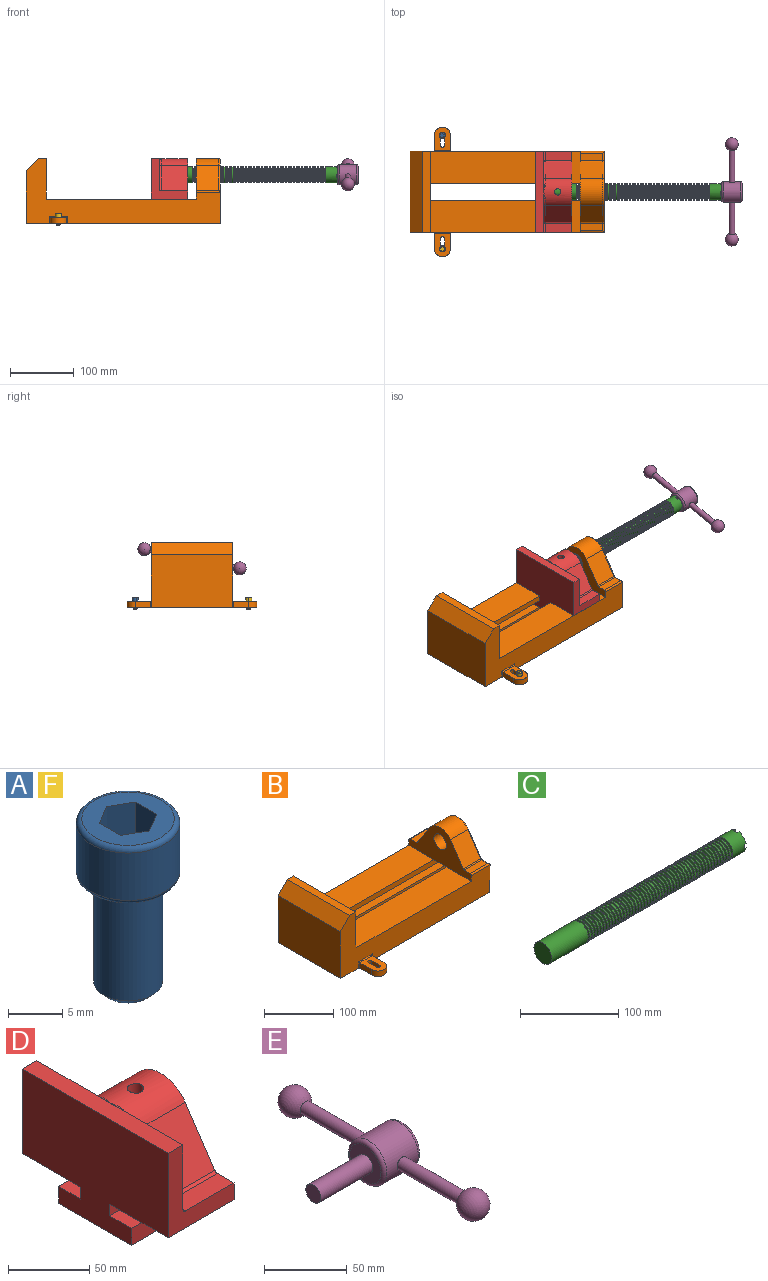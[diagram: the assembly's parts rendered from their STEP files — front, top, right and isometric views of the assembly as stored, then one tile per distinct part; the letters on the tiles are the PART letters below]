
ASSEMBLY  parts=6 mates=6
PART A: 15 faces, bbox 10.3x10.3x19.1 mm
  f0: plane 8.51x8.51mm, normal (0,0,1), area 37.2mm2, adj f5,f6,f7,f8,f9,f10,f14
  f1: cylinder r=3.17mm len=11.94mm, axis (0,0,1), area 238.2mm2, adj f4,f12
  f2: plane 4.83x4.83mm, normal (0,0,-1), area 18.3mm2, adj f12
  f3: cylinder r=4.76mm len=9.53mm, axis (0,0,-1), area 159.6mm2, adj f13,f14
  f4: plane 8.51x8.51mm, normal (0,0,-1), area 25.2mm2, adj f1,f13
  f5: plane 4.83x2.38mm, normal (-0.5,-0.87,0), area 13.3mm2, adj f0,f6,f10,f11
  f6: plane 4.83x2.38mm, normal (0.5,-0.87,0), area 13.3mm2, adj f0,f5,f7,f11
  f7: plane 4.83x2.75mm, normal (1,0,0), area 13.3mm2, adj f0,f6,f8,f11
  f8: plane 4.83x2.38mm, normal (0.5,0.87,0), area 13.3mm2, adj f0,f7,f9,f11
  f9: plane 4.83x2.38mm, normal (-0.5,0.87,0), area 13.3mm2, adj f0,f8,f10,f11
  f10: plane 4.83x2.75mm, normal (-1,0,0), area 13.3mm2, adj f0,f5,f9,f11
  f11: plane 5.5x4.76mm, normal (0,0,1), area 19.6mm2, adj f5,f6,f7,f8,f9,f10
  f12: cone r=3.17mm half-angle=45deg, axis (0,0,1), area 18.9mm2, adj f1,f2
  f13: torus R=4.25mm, axis (0,0,1), area 23mm2, adj f3,f4
  f14: torus R=4.25mm, axis (0,0,1), area 23mm2, adj f0,f3
PART B: 61 faces, bbox 304.8x203.2x103.7 mm
  f0: plane 304.8x101.6mm, normal (0,1,0), area 13520.3mm2, adj f3,f4,f5,f6,f7,f8,f9,f16
  f1: plane 304.8x101.6mm, normal (0,-1,0), area 13520.3mm2, adj f2,f3,f5,f6,f7,f8,f9,f16
  f2: plane 234.95x50.8mm, normal (0,0,1), area 11935.5mm2, adj f1,f5,f16,f26
  f3: plane 127x99.06mm, normal (1,0,0), area 7097.5mm2, adj f0,f1,f9,f14,f17,f18,f19,f20
  f4: plane 234.95x50.8mm, normal (0,0,1), area 11935.5mm2, adj f0,f5,f16,f27
  f5: plane 127x101.6mm, normal (1,0,0), area 9516.1mm2, adj f0,f1,f2,f4,f6,f9,f18,f19
  f6: plane 127x12.7mm, normal (0,0,1), area 1612.9mm2, adj f0,f1,f5,f7
  f7: plane 127x19.05mm, normal (-0.71,0,0.71), area 3421.5mm2, adj f0,f1,f6,f8
  f8: plane 127x82.55mm, normal (-1,0,0), area 10483.8mm2, adj f0,f1,f7,f9
  f9: plane 304.8x203.2mm, normal (0,0,-1), area 33298.3mm2, adj f0,f1,f3,f5,f8,f21,f22,f39
  f10: plane 35.56x11.98mm, normal (0,0,1), area 426mm2, adj f16,f28,f29,f30
  f11: plane 38.43x35.56mm, normal (0,0.83,0.56), area 1645.4mm2, adj f12,f16,f29,f32
  f12: cylinder r=25.4mm len=42.19mm, axis (1,0,0), area 1770.2mm2, adj f11,f13,f16,f33
  f13: plane 38.43x35.56mm, normal (0,-0.83,0.56), area 1645.4mm2, adj f12,f16,f34,f35
  f14: cylinder r=12.7mm len=38.1mm, axis (1,0,0), area 3040.2mm2, adj f3,f16
  f15: plane 35.56x11.98mm, normal (0,0,1), area 426mm2, adj f16,f34,f36,f38
  f16: plane 127x63.5mm, normal (-1,0,0), area 4155.5mm2, adj f0,f1,f2,f4,f10,f11,f12,f13
  f17: plane 38.1x25.4mm, normal (0,0,-1), area 967.7mm2, adj f3,f16,f26,f27
  f18: plane 273.05x19.05mm, normal (0,0,-1), area 5201.6mm2, adj f3,f5,f19,f26
  f19: plane 273.05x12.7mm, normal (0,1,0), area 3467.7mm2, adj f3,f5,f18,f20
  f20: plane 273.05x19.05mm, normal (0,0,1), area 5201.6mm2, adj f3,f5,f19,f21
  f21: plane 273.05x16.51mm, normal (0,1,0), area 4508.1mm2, adj f3,f5,f9,f20
  f22: plane 273.05x16.51mm, normal (0,-1,0), area 4508.1mm2, adj f3,f5,f9,f23
  f23: plane 273.05x19.05mm, normal (0,0,1), area 5201.6mm2, adj f3,f5,f22,f24
  f24: plane 273.05x12.7mm, normal (0,-1,0), area 3467.7mm2, adj f3,f5,f23,f25
  f25: plane 273.05x19.05mm, normal (0,0,-1), area 5201.6mm2, adj f3,f5,f24,f27
  f26: plane 273.05x8.89mm, normal (0,1,0), area 2427.4mm2, adj f2,f3,f5,f17,f18
  f27: plane 273.05x8.89mm, normal (0,-1,0), area 2427.4mm2, adj f3,f4,f5,f17,f25
  f28: cylinder r=2.54mm len=38.1mm, axis (1,0,0), area 148.3mm2, adj f0,f10,f16,f30
  f29: cylinder r=2.54mm len=35.56mm, axis (-1,0,0), area 88.5mm2, adj f10,f11,f16,f31
  f30: cylinder r=2.54mm len=14.52mm, axis (0,1,0), area 54.3mm2, adj f3,f10,f28,f31
  f31: torus R=5.08mm, axis (-1,0,0), area 13.5mm2, adj f3,f29,f30,f32
  f32: cylinder r=2.54mm len=39.84mm, axis (0,0.56,-0.83), area 184.6mm2, adj f3,f11,f31,f33
  f33: torus R=22.86mm, axis (-1,0,0), area 191.4mm2, adj f3,f12,f32,f35
  f34: cylinder r=2.54mm len=35.56mm, axis (-1,0,0), area 88.5mm2, adj f13,f15,f16,f37
  f35: cylinder r=2.54mm len=39.84mm, axis (0,0.56,0.83), area 184.6mm2, adj f3,f13,f33,f37
  f36: cylinder r=2.54mm len=38.1mm, axis (-1,0,0), area 148.3mm2, adj f1,f15,f16,f38
  f37: torus R=5.08mm, axis (-1,0,0), area 13.5mm2, adj f3,f34,f35,f38
  f38: cylinder r=2.54mm len=14.52mm, axis (0,1,0), area 54.3mm2, adj f3,f15,f36,f37
  f39: plane 23.88x9.53mm, normal (-1,0,0), area 227.4mm2, adj f9,f45,f46,f60
  f40: plane 23.88x9.53mm, normal (1,0,0), area 227.4mm2, adj f9,f45,f46,f58
  f41: cylinder r=3.3mm len=9.53mm, axis (0,0,-1), area 98.8mm2, adj f9,f42,f44,f46
  f42: plane 15.62x9.53mm, normal (-1,0,0), area 148.8mm2, adj f9,f41,f43,f46
  f43: cylinder r=3.3mm len=9.53mm, axis (0,0,-1), area 98.8mm2, adj f9,f42,f44,f46
  f44: plane 15.62x9.53mm, normal (1,0,0), area 148.8mm2, adj f9,f41,f43,f46
  f45: cylinder r=12.7mm len=25.4mm, axis (0,0,-1), area 380mm2, adj f9,f39,f40,f46
  f46: plane 36.58x25.4mm, normal (0,0,1), area 722.4mm2, adj f39,f40,f41,f42,f43,f44,f45,f59
  f47: plane 23.88x9.53mm, normal (-1,0,0), area 227.4mm2, adj f9,f53,f54,f56
  f48: plane 23.88x9.53mm, normal (1,0,0), area 227.4mm2, adj f9,f53,f54,f55
  f49: cylinder r=3.3mm len=9.53mm, axis (0,0,-1), area 98.8mm2, adj f9,f50,f52,f54
  f50: plane 15.62x9.53mm, normal (-1,0,0), area 148.8mm2, adj f9,f49,f51,f54
  f51: cylinder r=3.3mm len=9.53mm, axis (0,0,-1), area 98.8mm2, adj f9,f50,f52,f54
  f52: plane 15.62x9.53mm, normal (1,0,0), area 148.8mm2, adj f9,f49,f51,f54
  f53: cylinder r=12.7mm len=25.4mm, axis (0,0,-1), area 380mm2, adj f9,f47,f48,f54
  f54: plane 36.58x25.4mm, normal (0,0,1), area 722.4mm2, adj f47,f48,f49,f50,f51,f52,f53,f57
  f55: cylinder r=1.52mm len=11.05mm, axis (0,0,-1), area 24.1mm2, adj f0,f9,f48,f57
  f56: cylinder r=1.52mm len=11.05mm, axis (0,0,1), area 24.1mm2, adj f0,f9,f47,f57
  f57: cylinder r=1.52mm len=28.45mm, axis (1,0,0), area 63.5mm2, adj f0,f54,f55,f56
  f58: cylinder r=1.52mm len=11.05mm, axis (0,0,1), area 24.1mm2, adj f1,f9,f40,f59
  f59: cylinder r=1.52mm len=28.45mm, axis (-1,0,0), area 63.5mm2, adj f1,f46,f58,f60
  f60: cylinder r=1.52mm len=11.05mm, axis (0,0,-1), area 24.1mm2, adj f1,f9,f39,f59
PART C: 220 faces, bbox 279.4x25.4x25.4 mm
  f0: cylinder r=12.7mm len=25.4mm, axis (-1,0,0), area 1468.2mm2, adj f1,f2,f3,f5,f7,f208,f209,f210
  f1: plane 9.9x9.9mm, normal (1,0,0), area 62.3mm2, adj f0,f4,f213,f216
  f2: plane 9.9x9.9mm, normal (1,0,0), area 62.3mm2, adj f0,f4,f210,f218
  f3: plane 9.9x9.9mm, normal (1,0,0), area 62.3mm2, adj f0,f4,f209,f212
  f4: cylinder r=6.35mm len=25.4mm, axis (1,0,0), area 960.3mm2, adj f1,f2,f3,f5,f6,f208,f209,f210
  f5: plane 9.9x9.9mm, normal (1,0,0), area 62.3mm2, adj f0,f4,f215,f217
  f6: plane 12.7x12.7mm, normal (1,0,0), area 126.7mm2, adj f4
  f7: cone r=12.7mm half-angle=76deg, axis (1,0,0), area 188mm2, adj f0,f9
  f8: cone r=10.16mm half-angle=76deg, axis (-1,0,0), area 188mm2, adj f9,f10
  f9: cylinder r=10.16mm len=20.32mm, axis (1,0,0), area 81.1mm2, adj f7,f8
  f10: cylinder r=12.7mm len=25.4mm, axis (-1,0,0), area 131.7mm2, adj f8,f11
  f11: cone r=12.7mm half-angle=76deg, axis (1,0,0), area 188mm2, adj f10,f13
  f12: cone r=10.16mm half-angle=76deg, axis (-1,0,0), area 188mm2, adj f13,f14
  f13: cylinder r=10.16mm len=20.32mm, axis (1,0,0), area 81.1mm2, adj f11,f12
  f14: cylinder r=12.7mm len=25.4mm, axis (-1,0,0), area 131.7mm2, adj f12,f15
  f15: cone r=12.7mm half-angle=76deg, axis (1,0,0), area 188mm2, adj f14,f17
  f16: cone r=10.16mm half-angle=76deg, axis (-1,0,0), area 188mm2, adj f17,f18
  f17: cylinder r=10.16mm len=20.32mm, axis (1,0,0), area 81.1mm2, adj f15,f16
  f18: cylinder r=12.7mm len=25.4mm, axis (-1,0,0), area 131.7mm2, adj f16,f19
  f19: cone r=12.7mm half-angle=76deg, axis (1,0,0), area 188mm2, adj f18,f21
  f20: cone r=10.16mm half-angle=76deg, axis (-1,0,0), area 188mm2, adj f21,f22
  f21: cylinder r=10.16mm len=20.32mm, axis (1,0,0), area 81.1mm2, adj f19,f20
  f22: cylinder r=12.7mm len=25.4mm, axis (-1,0,0), area 131.7mm2, adj f20,f23
  f23: cone r=12.7mm half-angle=76deg, axis (1,0,0), area 188mm2, adj f22,f25
  f24: cone r=10.16mm half-angle=76deg, axis (-1,0,0), area 188mm2, adj f25,f26
  f25: cylinder r=10.16mm len=20.32mm, axis (1,0,0), area 81.1mm2, adj f23,f24
  f26: cylinder r=12.7mm len=25.4mm, axis (-1,0,0), area 131.7mm2, adj f24,f27
  f27: cone r=12.7mm half-angle=76deg, axis (1,0,0), area 188mm2, adj f26,f29
  f28: cone r=10.16mm half-angle=76deg, axis (-1,0,0), area 188mm2, adj f29,f30
  f29: cylinder r=10.16mm len=20.32mm, axis (1,0,0), area 81.1mm2, adj f27,f28
  f30: cylinder r=12.7mm len=25.4mm, axis (-1,0,0), area 131.7mm2, adj f28,f31
  f31: cone r=12.7mm half-angle=76deg, axis (1,0,0), area 188mm2, adj f30,f33
  f32: cone r=10.16mm half-angle=76deg, axis (-1,0,0), area 188mm2, adj f33,f34
  f33: cylinder r=10.16mm len=20.32mm, axis (1,0,0), area 81.1mm2, adj f31,f32
  f34: cylinder r=12.7mm len=25.4mm, axis (-1,0,0), area 131.7mm2, adj f32,f35
  f35: cone r=12.7mm half-angle=76deg, axis (1,0,0), area 188mm2, adj f34,f37
  f36: cone r=10.16mm half-angle=76deg, axis (-1,0,0), area 188mm2, adj f37,f38
  f37: cylinder r=10.16mm len=20.32mm, axis (1,0,0), area 81.1mm2, adj f35,f36
  f38: cylinder r=12.7mm len=25.4mm, axis (-1,0,0), area 131.7mm2, adj f36,f39
  f39: cone r=12.7mm half-angle=76deg, axis (1,0,0), area 188mm2, adj f38,f41
  f40: cone r=10.16mm half-angle=76deg, axis (-1,0,0), area 188mm2, adj f41,f42
  f41: cylinder r=10.16mm len=20.32mm, axis (1,0,0), area 81.1mm2, adj f39,f40
  f42: cylinder r=12.7mm len=25.4mm, axis (-1,0,0), area 131.7mm2, adj f40,f43
  f43: cone r=12.7mm half-angle=76deg, axis (1,0,0), area 188mm2, adj f42,f45
  f44: cone r=10.16mm half-angle=76deg, axis (-1,0,0), area 188mm2, adj f45,f46
  f45: cylinder r=10.16mm len=20.32mm, axis (1,0,0), area 81.1mm2, adj f43,f44
  f46: cylinder r=12.7mm len=25.4mm, axis (-1,0,0), area 131.7mm2, adj f44,f47
  f47: cone r=12.7mm half-angle=76deg, axis (1,0,0), area 188mm2, adj f46,f49
  f48: cone r=10.16mm half-angle=76deg, axis (-1,0,0), area 188mm2, adj f49,f50
  f49: cylinder r=10.16mm len=20.32mm, axis (1,0,0), area 81.1mm2, adj f47,f48
  f50: cylinder r=12.7mm len=25.4mm, axis (-1,0,0), area 131.7mm2, adj f48,f51
  f51: cone r=12.7mm half-angle=76deg, axis (1,0,0), area 188mm2, adj f50,f53
  f52: cone r=10.16mm half-angle=76deg, axis (-1,0,0), area 188mm2, adj f53,f54
  f53: cylinder r=10.16mm len=20.32mm, axis (1,0,0), area 81.1mm2, adj f51,f52
  f54: cylinder r=12.7mm len=25.4mm, axis (-1,0,0), area 131.7mm2, adj f52,f55
  f55: cone r=12.7mm half-angle=76deg, axis (1,0,0), area 188mm2, adj f54,f57
  f56: cone r=10.16mm half-angle=76deg, axis (-1,0,0), area 188mm2, adj f57,f58
  f57: cylinder r=10.16mm len=20.32mm, axis (1,0,0), area 81.1mm2, adj f55,f56
  f58: cylinder r=12.7mm len=25.4mm, axis (-1,0,0), area 131.7mm2, adj f56,f59
  f59: cone r=12.7mm half-angle=76deg, axis (1,0,0), area 188mm2, adj f58,f61
  f60: cone r=10.16mm half-angle=76deg, axis (-1,0,0), area 188mm2, adj f61,f62
  f61: cylinder r=10.16mm len=20.32mm, axis (1,0,0), area 81.1mm2, adj f59,f60
  f62: cylinder r=12.7mm len=25.4mm, axis (-1,0,0), area 131.7mm2, adj f60,f63
  f63: cone r=12.7mm half-angle=76deg, axis (1,0,0), area 188mm2, adj f62,f65
  f64: cone r=10.16mm half-angle=76deg, axis (-1,0,0), area 188mm2, adj f65,f66
  f65: cylinder r=10.16mm len=20.32mm, axis (1,0,0), area 81.1mm2, adj f63,f64
  f66: cylinder r=12.7mm len=25.4mm, axis (-1,0,0), area 131.7mm2, adj f64,f67
  f67: cone r=12.7mm half-angle=76deg, axis (1,0,0), area 188mm2, adj f66,f69
  f68: cone r=10.16mm half-angle=76deg, axis (-1,0,0), area 188mm2, adj f69,f70
  f69: cylinder r=10.16mm len=20.32mm, axis (1,0,0), area 81.1mm2, adj f67,f68
  f70: cylinder r=12.7mm len=25.4mm, axis (-1,0,0), area 131.7mm2, adj f68,f71
  f71: cone r=12.7mm half-angle=76deg, axis (1,0,0), area 188mm2, adj f70,f73
  f72: cone r=10.16mm half-angle=76deg, axis (-1,0,0), area 188mm2, adj f73,f74
  f73: cylinder r=10.16mm len=20.32mm, axis (1,0,0), area 81.1mm2, adj f71,f72
  f74: cylinder r=12.7mm len=25.4mm, axis (-1,0,0), area 131.7mm2, adj f72,f75
  f75: cone r=12.7mm half-angle=76deg, axis (1,0,0), area 188mm2, adj f74,f77
  f76: cone r=10.16mm half-angle=76deg, axis (-1,0,0), area 188mm2, adj f77,f78
  f77: cylinder r=10.16mm len=20.32mm, axis (1,0,0), area 81.1mm2, adj f75,f76
  f78: cylinder r=12.7mm len=25.4mm, axis (-1,0,0), area 131.7mm2, adj f76,f79
  f79: cone r=12.7mm half-angle=76deg, axis (1,0,0), area 188mm2, adj f78,f81
  f80: cone r=10.16mm half-angle=76deg, axis (-1,0,0), area 188mm2, adj f81,f82
  f81: cylinder r=10.16mm len=20.32mm, axis (1,0,0), area 81.1mm2, adj f79,f80
  f82: cylinder r=12.7mm len=25.4mm, axis (-1,0,0), area 131.7mm2, adj f80,f83
  f83: cone r=12.7mm half-angle=76deg, axis (1,0,0), area 188mm2, adj f82,f85
  f84: cone r=10.16mm half-angle=76deg, axis (-1,0,0), area 188mm2, adj f85,f86
  f85: cylinder r=10.16mm len=20.32mm, axis (1,0,0), area 81.1mm2, adj f83,f84
  f86: cylinder r=12.7mm len=25.4mm, axis (-1,0,0), area 131.7mm2, adj f84,f87
  f87: cone r=12.7mm half-angle=76deg, axis (1,0,0), area 188mm2, adj f86,f89
  f88: cone r=10.16mm half-angle=76deg, axis (-1,0,0), area 188mm2, adj f89,f90
  f89: cylinder r=10.16mm len=20.32mm, axis (1,0,0), area 81.1mm2, adj f87,f88
  f90: cylinder r=12.7mm len=25.4mm, axis (-1,0,0), area 131.7mm2, adj f88,f91
  f91: cone r=12.7mm half-angle=76deg, axis (1,0,0), area 188mm2, adj f90,f93
  f92: cone r=10.16mm half-angle=76deg, axis (-1,0,0), area 188mm2, adj f93,f94
  f93: cylinder r=10.16mm len=20.32mm, axis (1,0,0), area 81.1mm2, adj f91,f92
  f94: cylinder r=12.7mm len=25.4mm, axis (-1,0,0), area 131.7mm2, adj f92,f95
  f95: cone r=12.7mm half-angle=76deg, axis (1,0,0), area 188mm2, adj f94,f97
  f96: cone r=10.16mm half-angle=76deg, axis (-1,0,0), area 188mm2, adj f97,f98
  f97: cylinder r=10.16mm len=20.32mm, axis (1,0,0), area 81.1mm2, adj f95,f96
  f98: cylinder r=12.7mm len=25.4mm, axis (-1,0,0), area 131.7mm2, adj f96,f99
  f99: cone r=12.7mm half-angle=76deg, axis (1,0,0), area 188mm2, adj f98,f101
  f100: cone r=10.16mm half-angle=76deg, axis (-1,0,0), area 188mm2, adj f101,f102
  f101: cylinder r=10.16mm len=20.32mm, axis (1,0,0), area 81.1mm2, adj f99,f100
  f102: cylinder r=12.7mm len=25.4mm, axis (-1,0,0), area 131.7mm2, adj f100,f103
  f103: cone r=12.7mm half-angle=76deg, axis (1,0,0), area 188mm2, adj f102,f105
  f104: cone r=10.16mm half-angle=76deg, axis (-1,0,0), area 188mm2, adj f105,f106
  f105: cylinder r=10.16mm len=20.32mm, axis (1,0,0), area 81.1mm2, adj f103,f104
  f106: cylinder r=12.7mm len=25.4mm, axis (-1,0,0), area 131.7mm2, adj f104,f107
  f107: cone r=12.7mm half-angle=76deg, axis (1,0,0), area 188mm2, adj f106,f109
  f108: cone r=10.16mm half-angle=76deg, axis (-1,0,0), area 188mm2, adj f109,f110
  f109: cylinder r=10.16mm len=20.32mm, axis (1,0,0), area 81.1mm2, adj f107,f108
  f110: cylinder r=12.7mm len=25.4mm, axis (-1,0,0), area 131.7mm2, adj f108,f111
  f111: cone r=12.7mm half-angle=76deg, axis (1,0,0), area 188mm2, adj f110,f113
  f112: cone r=10.16mm half-angle=76deg, axis (-1,0,0), area 188mm2, adj f113,f114
  f113: cylinder r=10.16mm len=20.32mm, axis (1,0,0), area 81.1mm2, adj f111,f112
  f114: cylinder r=12.7mm len=25.4mm, axis (-1,0,0), area 131.7mm2, adj f112,f115
  f115: cone r=12.7mm half-angle=76deg, axis (1,0,0), area 188mm2, adj f114,f117
  f116: cone r=10.16mm half-angle=76deg, axis (-1,0,0), area 188mm2, adj f117,f118
  f117: cylinder r=10.16mm len=20.32mm, axis (1,0,0), area 81.1mm2, adj f115,f116
  f118: cylinder r=12.7mm len=25.4mm, axis (-1,0,0), area 131.7mm2, adj f116,f119
  f119: cone r=12.7mm half-angle=76deg, axis (1,0,0), area 188mm2, adj f118,f121
  f120: cone r=10.16mm half-angle=76deg, axis (-1,0,0), area 188mm2, adj f121,f122
  f121: cylinder r=10.16mm len=20.32mm, axis (1,0,0), area 81.1mm2, adj f119,f120
  f122: cylinder r=12.7mm len=25.4mm, axis (-1,0,0), area 131.7mm2, adj f120,f123
  f123: cone r=12.7mm half-angle=76deg, axis (1,0,0), area 188mm2, adj f122,f125
  f124: cone r=10.16mm half-angle=76deg, axis (-1,0,0), area 188mm2, adj f125,f126
  f125: cylinder r=10.16mm len=20.32mm, axis (1,0,0), area 81.1mm2, adj f123,f124
  f126: cylinder r=12.7mm len=25.4mm, axis (-1,0,0), area 131.7mm2, adj f124,f127
  f127: cone r=12.7mm half-angle=76deg, axis (1,0,0), area 188mm2, adj f126,f129
  f128: cone r=10.16mm half-angle=76deg, axis (-1,0,0), area 188mm2, adj f129,f130
  f129: cylinder r=10.16mm len=20.32mm, axis (1,0,0), area 81.1mm2, adj f127,f128
  f130: cylinder r=12.7mm len=25.4mm, axis (-1,0,0), area 131.7mm2, adj f128,f131
  f131: cone r=12.7mm half-angle=76deg, axis (1,0,0), area 188mm2, adj f130,f133
  f132: cone r=10.16mm half-angle=76deg, axis (-1,0,0), area 188mm2, adj f133,f134
  f133: cylinder r=10.16mm len=20.32mm, axis (1,0,0), area 81.1mm2, adj f131,f132
  f134: cylinder r=12.7mm len=25.4mm, axis (-1,0,0), area 131.7mm2, adj f132,f135
  f135: cone r=12.7mm half-angle=76deg, axis (1,0,0), area 188mm2, adj f134,f137
  f136: cone r=10.16mm half-angle=76deg, axis (-1,0,0), area 188mm2, adj f137,f138
  f137: cylinder r=10.16mm len=20.32mm, axis (1,0,0), area 81.1mm2, adj f135,f136
  f138: cylinder r=12.7mm len=25.4mm, axis (-1,0,0), area 131.7mm2, adj f136,f139
  f139: cone r=12.7mm half-angle=76deg, axis (1,0,0), area 188mm2, adj f138,f141
  f140: cone r=10.16mm half-angle=76deg, axis (-1,0,0), area 188mm2, adj f141,f142
  f141: cylinder r=10.16mm len=20.32mm, axis (1,0,0), area 81.1mm2, adj f139,f140
  f142: cylinder r=12.7mm len=25.4mm, axis (-1,0,0), area 131.7mm2, adj f140,f143
  f143: cone r=12.7mm half-angle=76deg, axis (1,0,0), area 188mm2, adj f142,f145
  f144: cone r=10.16mm half-angle=76deg, axis (-1,0,0), area 188mm2, adj f145,f146
  f145: cylinder r=10.16mm len=20.32mm, axis (1,0,0), area 81.1mm2, adj f143,f144
  f146: cylinder r=12.7mm len=25.4mm, axis (-1,0,0), area 131.7mm2, adj f144,f147
  f147: cone r=12.7mm half-angle=76deg, axis (1,0,0), area 188mm2, adj f146,f149
  f148: cone r=10.16mm half-angle=76deg, axis (-1,0,0), area 188mm2, adj f149,f150
  f149: cylinder r=10.16mm len=20.32mm, axis (1,0,0), area 81.1mm2, adj f147,f148
  f150: cylinder r=12.7mm len=25.4mm, axis (-1,0,0), area 131.7mm2, adj f148,f151
  f151: cone r=12.7mm half-angle=76deg, axis (1,0,0), area 188mm2, adj f150,f153
  f152: cone r=10.16mm half-angle=76deg, axis (-1,0,0), area 188mm2, adj f153,f154
  f153: cylinder r=10.16mm len=20.32mm, axis (1,0,0), area 81.1mm2, adj f151,f152
  f154: cylinder r=12.7mm len=25.4mm, axis (-1,0,0), area 131.7mm2, adj f152,f155
  f155: cone r=12.7mm half-angle=76deg, axis (1,0,0), area 188mm2, adj f154,f157
  f156: cone r=10.16mm half-angle=76deg, axis (-1,0,0), area 188mm2, adj f157,f158
  f157: cylinder r=10.16mm len=20.32mm, axis (1,0,0), area 81.1mm2, adj f155,f156
  f158: cylinder r=12.7mm len=25.4mm, axis (-1,0,0), area 131.7mm2, adj f156,f159
  f159: cone r=12.7mm half-angle=76deg, axis (1,0,0), area 188mm2, adj f158,f161
  f160: cone r=10.16mm half-angle=76deg, axis (-1,0,0), area 188mm2, adj f161,f162
  f161: cylinder r=10.16mm len=20.32mm, axis (1,0,0), area 81.1mm2, adj f159,f160
  f162: cylinder r=12.7mm len=25.4mm, axis (-1,0,0), area 131.7mm2, adj f160,f163
  f163: cone r=12.7mm half-angle=76deg, axis (1,0,0), area 188mm2, adj f162,f165
  f164: cone r=10.16mm half-angle=76deg, axis (-1,0,0), area 188mm2, adj f165,f166
  f165: cylinder r=10.16mm len=20.32mm, axis (1,0,0), area 81.1mm2, adj f163,f164
  f166: cylinder r=12.7mm len=25.4mm, axis (-1,0,0), area 131.7mm2, adj f164,f167
  f167: cone r=12.7mm half-angle=76deg, axis (1,0,0), area 188mm2, adj f166,f169
  f168: cone r=10.16mm half-angle=76deg, axis (-1,0,0), area 188mm2, adj f169,f170
  f169: cylinder r=10.16mm len=20.32mm, axis (1,0,0), area 81.1mm2, adj f167,f168
  f170: cylinder r=12.7mm len=25.4mm, axis (-1,0,0), area 131.7mm2, adj f168,f171
  f171: cone r=12.7mm half-angle=76deg, axis (1,0,0), area 188mm2, adj f170,f173
  f172: cone r=10.16mm half-angle=76deg, axis (-1,0,0), area 188mm2, adj f173,f174
  f173: cylinder r=10.16mm len=20.32mm, axis (1,0,0), area 81.1mm2, adj f171,f172
  f174: cylinder r=12.7mm len=25.4mm, axis (-1,0,0), area 131.7mm2, adj f172,f175
  f175: cone r=12.7mm half-angle=76deg, axis (1,0,0), area 188mm2, adj f174,f177
  f176: cone r=10.16mm half-angle=76deg, axis (-1,0,0), area 188mm2, adj f177,f178
  f177: cylinder r=10.16mm len=20.32mm, axis (1,0,0), area 81.1mm2, adj f175,f176
  f178: cylinder r=12.7mm len=25.4mm, axis (-1,0,0), area 131.7mm2, adj f176,f179
  f179: cone r=12.7mm half-angle=76deg, axis (1,0,0), area 188mm2, adj f178,f181
  f180: cone r=10.16mm half-angle=76deg, axis (-1,0,0), area 188mm2, adj f181,f182
  f181: cylinder r=10.16mm len=20.32mm, axis (1,0,0), area 81.1mm2, adj f179,f180
  f182: cylinder r=12.7mm len=25.4mm, axis (-1,0,0), area 131.7mm2, adj f180,f183
  f183: cone r=12.7mm half-angle=76deg, axis (1,0,0), area 188mm2, adj f182,f185
  f184: cone r=10.16mm half-angle=76deg, axis (-1,0,0), area 188mm2, adj f185,f186
  f185: cylinder r=10.16mm len=20.32mm, axis (1,0,0), area 81.1mm2, adj f183,f184
  f186: cylinder r=12.7mm len=25.4mm, axis (-1,0,0), area 131.7mm2, adj f184,f187
  f187: cone r=12.7mm half-angle=76deg, axis (1,0,0), area 188mm2, adj f186,f189
  f188: cone r=10.16mm half-angle=76deg, axis (-1,0,0), area 188mm2, adj f189,f190
  f189: cylinder r=10.16mm len=20.32mm, axis (1,0,0), area 81.1mm2, adj f187,f188
  f190: cylinder r=12.7mm len=25.4mm, axis (-1,0,0), area 131.7mm2, adj f188,f191
  f191: cone r=12.7mm half-angle=76deg, axis (1,0,0), area 188mm2, adj f190,f193
  f192: cone r=10.16mm half-angle=76deg, axis (-1,0,0), area 188mm2, adj f193,f194
  f193: cylinder r=10.16mm len=20.32mm, axis (1,0,0), area 81.1mm2, adj f191,f192
  f194: cylinder r=12.7mm len=25.4mm, axis (-1,0,0), area 131.7mm2, adj f192,f195
  f195: cone r=12.7mm half-angle=76deg, axis (1,0,0), area 188mm2, adj f194,f197
  f196: cone r=10.16mm half-angle=76deg, axis (-1,0,0), area 188mm2, adj f197,f198
  f197: cylinder r=10.16mm len=20.32mm, axis (1,0,0), area 81.1mm2, adj f195,f196
  f198: cylinder r=12.7mm len=25.4mm, axis (-1,0,0), area 131.7mm2, adj f196,f199
  f199: cone r=12.7mm half-angle=76deg, axis (1,0,0), area 188mm2, adj f198,f201
  f200: cone r=10.16mm half-angle=76deg, axis (-1,0,0), area 188mm2, adj f201,f202
  f201: cylinder r=10.16mm len=20.32mm, axis (1,0,0), area 81.1mm2, adj f199,f200
  f202: cylinder r=12.7mm len=25.4mm, axis (-1,0,0), area 131.7mm2, adj f200,f203
  f203: cone r=12.7mm half-angle=76deg, axis (1,0,0), area 188mm2, adj f202,f205
  f204: cone r=10.16mm half-angle=76deg, axis (-1,0,0), area 188mm2, adj f205,f207
  f205: cylinder r=10.16mm len=20.32mm, axis (1,0,0), area 81.1mm2, adj f203,f204
  f206: plane 25.4x25.4mm, normal (-1,0,0), area 506.7mm2, adj f207
  f207: cylinder r=12.7mm len=52.45mm, axis (-1,0,0), area 4185.4mm2, adj f204,f206
  f208: plane 6.88x5.08mm, normal (1,0,0), area 32.7mm2, adj f0,f4,f209,f210
  f209: plane 6.62x2.54mm, normal (0,-1,0), area 16.8mm2, adj f0,f3,f4,f208
  f210: plane 6.62x2.54mm, normal (0,1,0), area 16.8mm2, adj f0,f2,f4,f208
  f211: plane 6.88x5.08mm, normal (1,0,0), area 32.7mm2, adj f0,f4,f212,f213
  f212: plane 6.62x2.54mm, normal (0,0,1), area 16.8mm2, adj f0,f3,f4,f211
  f213: plane 6.62x2.54mm, normal (0,0,-1), area 16.8mm2, adj f0,f1,f4,f211
  f214: plane 6.88x5.08mm, normal (1,0,0), area 32.7mm2, adj f0,f4,f215,f216
  f215: plane 6.62x2.54mm, normal (0,1,0), area 16.8mm2, adj f0,f4,f5,f214
  f216: plane 6.62x2.54mm, normal (0,-1,0), area 16.8mm2, adj f0,f1,f4,f214
  f217: plane 6.62x2.54mm, normal (0,0,-1), area 16.8mm2, adj f0,f4,f5,f219
  f218: plane 6.62x2.54mm, normal (0,0,1), area 16.8mm2, adj f0,f2,f4,f219
  f219: plane 6.88x5.08mm, normal (1,0,0), area 32.7mm2, adj f0,f4,f217,f218
PART D: 36 faces, bbox 57.2x127x89 mm
  f0: plane 57.15x50.8mm, normal (0,0,-1), area 2903.2mm2, adj f6,f9,f10,f23
  f1: cylinder r=12.7mm len=44.45mm, axis (1,0,0), area 3464.3mm2, adj f6,f15,f16
  f2: plane 41.91x14.52mm, normal (0,0,1), area 608.5mm2, adj f6,f11,f24,f25
  f3: plane 51.86x48.26mm, normal (1,0,0), area 1495.7mm2, adj f8,f10,f31,f33,f35
  f4: plane 51.86x48.26mm, normal (1,0,0), area 1495.7mm2, adj f8,f11,f24,f28,f29
  f5: plane 57.15x50.8mm, normal (0,0,-1), area 2903.2mm2, adj f6,f9,f11,f22
  f6: plane 127x85.09mm, normal (1,0,0), area 5190.6mm2, adj f0,f1,f2,f5,f7,f10,f11,f12
  f7: plane 41.91x14.52mm, normal (0,0,1), area 608.5mm2, adj f6,f10,f30,f31
  f8: plane 127x12.7mm, normal (0,0,1), area 1612.9mm2, adj f3,f4,f9,f10,f11,f26,f34
  f9: plane 127x85.09mm, normal (-1,0,0), area 9096.8mm2, adj f0,f5,f8,f10,f11,f17,f18,f19
  f10: plane 63.5x57.15mm, normal (0,-1,0), area 1372.3mm2, adj f0,f3,f6,f7,f8,f9,f31
  f11: plane 63.5x57.15mm, normal (0,1,0), area 1372.3mm2, adj f2,f4,f5,f6,f8,f9,f24
  f12: plane 41.91x38.43mm, normal (0,-0.83,0.56), area 1939.2mm2, adj f6,f13,f30,f33
  f13: cylinder r=25.4mm len=44.45mm, axis (1,0,0), area 2026.5mm2, adj f6,f12,f14,f16,f26,f28,f34,f35
  f14: plane 41.91x38.43mm, normal (0,0.83,0.56), area 1939.2mm2, adj f6,f13,f25,f29
  f15: plane 25.4x25.4mm, normal (1,0,0), area 506.7mm2, adj f1
  f16: cylinder r=5.08mm len=13.76mm, axis (0,0,1), area 414mm2, adj f1,f13
  f17: plane 57.15x19.05mm, normal (0,0,1), area 1088.7mm2, adj f6,f9,f18,f23
  f18: plane 57.15x12.7mm, normal (0,-1,0), area 725.8mm2, adj f6,f9,f17,f19
  f19: plane 63.5x57.15mm, normal (0,0,-1), area 3629mm2, adj f6,f9,f18,f20
  f20: plane 57.15x12.7mm, normal (0,1,0), area 725.8mm2, adj f6,f9,f19,f21
  f21: plane 57.15x19.05mm, normal (0,0,1), area 1088.7mm2, adj f6,f9,f20,f22
  f22: plane 57.15x8.89mm, normal (0,1,0), area 508.1mm2, adj f5,f6,f9,f21
  f23: plane 57.15x8.89mm, normal (0,-1,0), area 508.1mm2, adj f0,f6,f9,f17
  f24: cylinder r=2.54mm len=14.52mm, axis (0,-1,0), area 57.9mm2, adj f2,f4,f11,f27
  f25: cylinder r=2.54mm len=41.91mm, axis (1,0,0), area 104.3mm2, adj f2,f6,f14,f27
  f26: bspline ~12.24x2.8mm, area 20.9mm2, adj f8,f13,f28
  f27: sphere r=2.54mm, area 6.3mm2, adj f24,f25,f29
  f28: torus R=27.94mm, axis (1,0,0), area 57.8mm2, adj f4,f13,f26,f29
  f29: cylinder r=2.54mm len=39.84mm, axis (0,-0.56,0.83), area 184.6mm2, adj f4,f14,f27,f28
  f30: cylinder r=2.54mm len=41.91mm, axis (1,0,0), area 104.3mm2, adj f6,f7,f12,f32
  f31: cylinder r=2.54mm len=14.52mm, axis (0,-1,0), area 57.9mm2, adj f3,f7,f10,f32
  f32: sphere r=2.54mm, area 6.3mm2, adj f30,f31,f33
  f33: cylinder r=2.54mm len=39.84mm, axis (0,-0.56,-0.83), area 184.6mm2, adj f3,f12,f32,f35
  f34: bspline ~12.24x2.8mm, area 20.9mm2, adj f8,f13,f35
  f35: torus R=27.94mm, axis (1,0,0), area 57.8mm2, adj f3,f13,f33,f34
PART E: 11 faces, bbox 76.2x172.7x34.4 mm
  f0: sphere r=10.16mm, area 1231.8mm2, adj f1
  f1: cylinder r=4.45mm len=51.82mm, axis (0,1,0), area 1438.5mm2, adj f0,f4
  f2: sphere r=10.16mm, area 1231.8mm2, adj f3
  f3: cylinder r=4.45mm len=51.82mm, axis (0,1,0), area 1438.5mm2, adj f2,f4
  f4: cylinder r=15.88mm len=31.75mm, axis (-1,0,0), area 2534.7mm2, adj f1,f3,f9,f10
  f5: cylinder r=6.35mm len=44.45mm, axis (-1,0,0), area 1773.5mm2, adj f6,f8
  f6: plane 12.7x12.7mm, normal (-1,0,0), area 126.7mm2, adj f5
  f7: plane 26.67x26.67mm, normal (1,0,0), area 558.6mm2, adj f10
  f8: plane 26.67x26.67mm, normal (-1,0,0), area 432mm2, adj f5,f9
  f9: torus R=13.33mm, axis (1,0,0), area 374.8mm2, adj f4,f8
  f10: torus R=13.33mm, axis (1,0,0), area 374.8mm2, adj f4,f7
PART F: same geometry as A
PLACE A rot(axis=(0,0,1),180deg) t=(19.05,101.6,9.53)mm
PLACE B t=(273.05,12.7,0)mm fixed
PLACE C rot(axis=(-1,0,0),168.7deg) t=(437.75,-2.28,150.91)mm
PLACE D t=(437.75,12.7,0)mm
PLACE E rot(axis=(1,0,0),11.3deg) t=(418.7,27.68,1.49)mm
PLACE F rot(axis=(0,0,1),90deg) t=(19.05,-76.2,9.53)mm
MATE cylindrical B.f12 <-> C.f7  axis (-1,0,0) through (234.95,12.7,76.2)mm
MATE fastened E.f5 <-> C.f4  axis (-1,0,0) through (456.8,12.7,76.2)mm
MATE slider D.f9 <-> B.f5  axis (-1,0,0) through (164.7,-50.8,38.1)mm
MATE pin_slot B.f49 <-> A.f1  axis (0,0,1) through (19.05,101.6,9.52)mm
MATE revolute C.f7 <-> D.f28  axis (-1,0,0) through (177.4,12.7,76.2)mm
MATE pin_slot B.f41 <-> F.f1  axis (0,0,1) through (19.05,-76.2,9.52)mm
